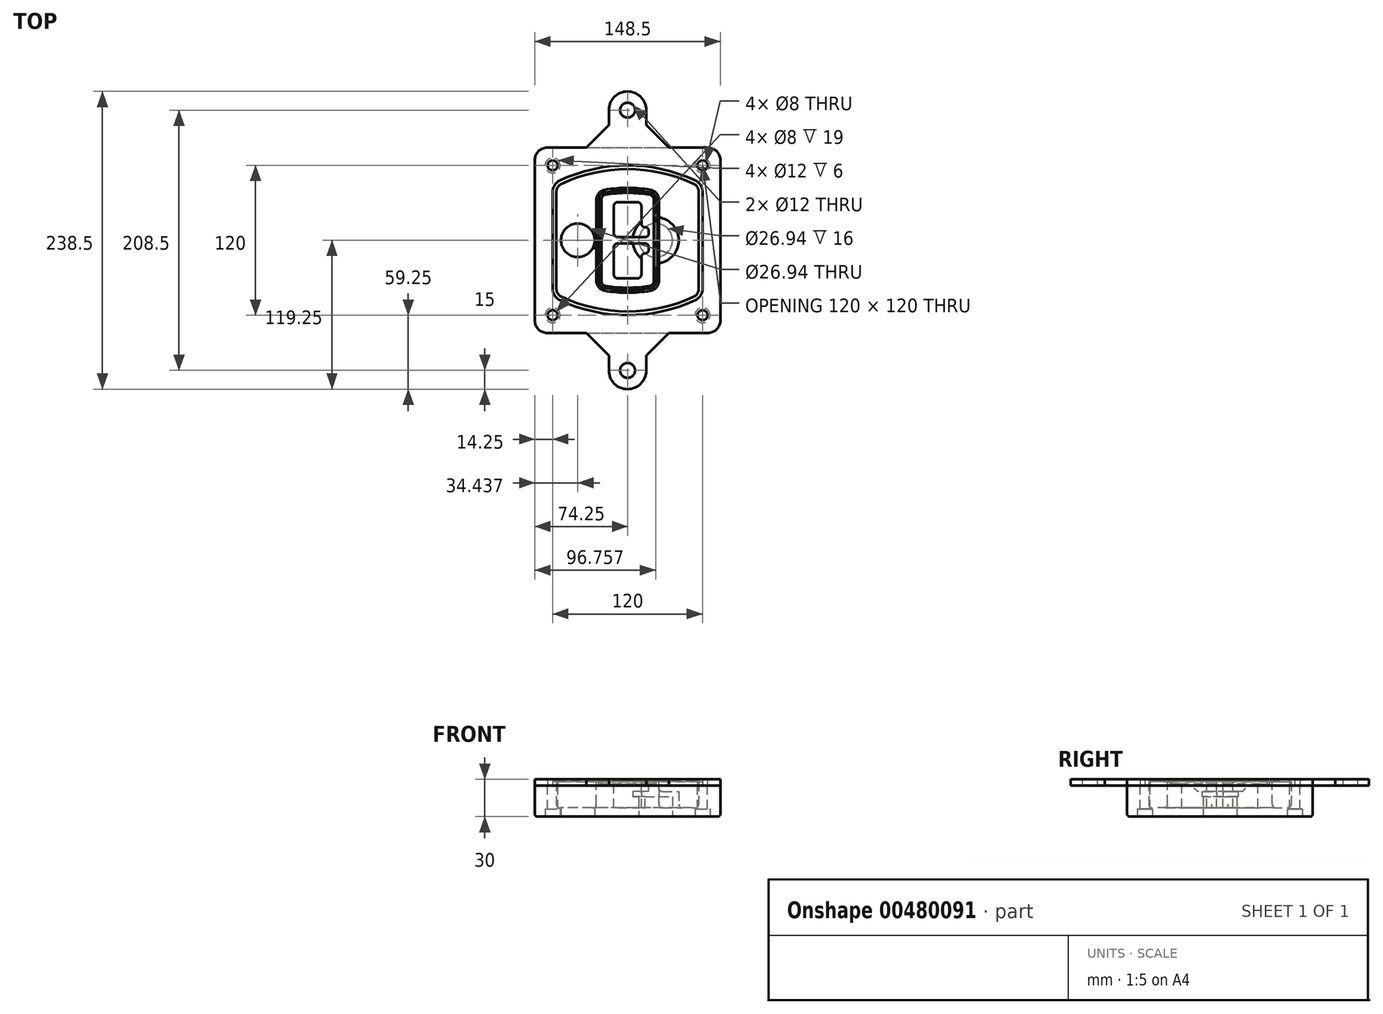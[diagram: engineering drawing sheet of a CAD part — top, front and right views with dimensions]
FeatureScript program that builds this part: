
annotation { "Feature Type Name" : "Feature", "Feature Type Description" : "" }
export const myFeature = defineFeature(function(context is Context, id is Id, definition is map)
    precondition{}
    {
        {
            var Q0;
            Q0=qCreatedBy(makeId("Top.planeOp"),FACE);
            var sketch = newSketch(context, id + "F0", { "sketchPlane" : qUnion([Q0])});
            skPoint(sketch, "E0.rect.middle", {"position": v(0, 0) * mm});
            skLineSegment(sketch, "E1.bottom", {"start": v(-64.25, -74.25) * mm, "end": v(64.25, -74.25) * mm});
            skLineSegment(sketch, "E1.top", {"start": v(-64.25, 74.25) * mm, "end": v(64.25, 74.25) * mm});
            skLineSegment(sketch, "E1.left", {"start": v(-74.25, -64.25) * mm, "end": v(-74.25, 64.25) * mm});
            skLineSegment(sketch, "E1.right", {"start": v(74.25, -64.25) * mm, "end": v(74.25, 64.25) * mm});
            skLineSegment(sketch, "E2", {"start": v(-74.25, 74.25) * mm, "end": v(74.25, -74.25) * mm, "construction": true});
            skLineSegment(sketch, "E3", {"start": v(74.25, 74.25) * mm, "end": v(-74.25, -74.25) * mm, "construction": true});
            skCircle(sketch, "E4", {"center": v(-60, 60) * mm, "radius": 4 * mm});
            skCircle(sketch, "E5", {"center": v(60, 60) * mm, "radius": 4 * mm});
            skCircle(sketch, "E6", {"center": v(60, -60) * mm, "radius": 4 * mm});
            skCircle(sketch, "E7", {"center": v(-60, -60) * mm, "radius": 4 * mm});
            skLineSegment(sketch, "E8", {"start": v(-60, 60) * mm, "end": v(60, 60) * mm, "construction": true});
            skLineSegment(sketch, "E9", {"start": v(60, 60) * mm, "end": v(60, -60) * mm, "construction": true});
            skLineSegment(sketch, "E10", {"start": v(60, -60) * mm, "end": v(-60, -60) * mm, "construction": true});
            skLineSegment(sketch, "E11", {"start": v(-60, -60) * mm, "end": v(-60, 60) * mm, "construction": true});
            skLineSegment(sketch, "E12", {"start": v(-60, 38.83) * mm, "end": v(-60, -38.83) * mm});
            skLineSegment(sketch, "E13", {"start": v(60, 38.83) * mm, "end": v(60, -38.83) * mm});
            skArc(sketch, "E14", {"start": v(54.26, 47.88) * mm, "mid": v(0, 60) * mm, "end": v(-54.26, 47.88) * mm});
            skArc(sketch, "E15", {"start": v(-54.26, -47.88) * mm, "mid": v(0, -60) * mm, "end": v(54.26, -47.88) * mm});
            skLineSegment(sketch, "E16", {"start": v(-60, 0) * mm, "end": v(60, 0) * mm, "construction": true});
            skPoint(sketch, "E17.visualSharp", {"position": v(-60, -45) * mm});
            skArc(sketch, "E17.filletArc", {"start": v(-60, -38.83) * mm, "mid": v(-58.44, -44.2) * mm, "end": v(-54.26, -47.88) * mm});
            skPoint(sketch, "E18.visualSharp", {"position": v(-60, 45) * mm});
            skArc(sketch, "E18.filletArc", {"start": v(-54.26, 47.88) * mm, "mid": v(-58.44, 44.2) * mm, "end": v(-60, 38.83) * mm});
            skPoint(sketch, "E19.visualSharp", {"position": v(60, 45) * mm});
            skArc(sketch, "E19.filletArc", {"start": v(60, 38.83) * mm, "mid": v(58.44, 44.2) * mm, "end": v(54.26, 47.88) * mm});
            skPoint(sketch, "E20.visualSharp", {"position": v(60, -45) * mm});
            skArc(sketch, "E20.filletArc", {"start": v(54.26, -47.88) * mm, "mid": v(58.44, -44.2) * mm, "end": v(60, -38.83) * mm});
            skPoint(sketch, "E21.visualSharp", {"position": v(-74.25, 74.25) * mm});
            skArc(sketch, "E21.filletArc", {"start": v(-64.25, 74.25) * mm, "mid": v(-71.32, 71.32) * mm, "end": v(-74.25, 64.25) * mm});
            skPoint(sketch, "E22.visualSharp", {"position": v(74.25, 74.25) * mm});
            skArc(sketch, "E22.filletArc", {"start": v(74.25, 64.25) * mm, "mid": v(71.32, 71.32) * mm, "end": v(64.25, 74.25) * mm});
            skPoint(sketch, "E23.visualSharp", {"position": v(74.25, -74.25) * mm});
            skArc(sketch, "E23.filletArc", {"start": v(64.25, -74.25) * mm, "mid": v(71.32, -71.32) * mm, "end": v(74.25, -64.25) * mm});
            skPoint(sketch, "E24.visualSharp", {"position": v(-74.25, -74.25) * mm});
            skArc(sketch, "E24.filletArc", {"start": v(-74.25, -64.25) * mm, "mid": v(-71.32, -71.32) * mm, "end": v(-64.25, -74.25) * mm});
            skArc(sketch, "E25.0", {"start": v(57, 38.83) * mm, "mid": v(55.9, 42.58) * mm, "end": v(52.98, 45.17) * mm});
            skLineSegment(sketch, "E25.1", {"start": v(57, 38.83) * mm, "end": v(57, -38.83) * mm});
            skArc(sketch, "E25.2", {"start": v(52.98, -45.17) * mm, "mid": v(55.9, -42.58) * mm, "end": v(57, -38.83) * mm});
            skArc(sketch, "E25.3", {"start": v(-52.98, -45.17) * mm, "mid": v(0, -57) * mm, "end": v(52.98, -45.17) * mm});
            skArc(sketch, "E25.4", {"start": v(-57, -38.83) * mm, "mid": v(-55.9, -42.58) * mm, "end": v(-52.98, -45.17) * mm});
            skArc(sketch, "E25.5", {"start": v(52.98, 45.17) * mm, "mid": v(0, 57) * mm, "end": v(-52.98, 45.17) * mm});
            skLineSegment(sketch, "E25.6", {"start": v(-57, 38.83) * mm, "end": v(-57, -38.83) * mm});
            skArc(sketch, "E25.7", {"start": v(-52.98, 45.17) * mm, "mid": v(-55.9, 42.58) * mm, "end": v(-57, 38.83) * mm});
            skArc(sketch, "E26.0", {"start": v(-55.96, 51.5) * mm, "mid": v(-61.82, 46.33) * mm, "end": v(-64, 38.83) * mm});
            skArc(sketch, "E26.1", {"start": v(55.96, 51.5) * mm, "mid": v(0, 64) * mm, "end": v(-55.96, 51.5) * mm});
            skArc(sketch, "E26.2", {"start": v(64, 38.83) * mm, "mid": v(61.82, 46.33) * mm, "end": v(55.96, 51.5) * mm});
            skLineSegment(sketch, "E26.3", {"start": v(64, 38.83) * mm, "end": v(64, -38.83) * mm});
            skArc(sketch, "E26.4", {"start": v(55.96, -51.5) * mm, "mid": v(61.82, -46.33) * mm, "end": v(64, -38.83) * mm});
            skLineSegment(sketch, "E26.5", {"start": v(-64, 38.83) * mm, "end": v(-64, -38.83) * mm});
            skArc(sketch, "E26.6", {"start": v(-55.96, -51.5) * mm, "mid": v(0, -64) * mm, "end": v(55.96, -51.5) * mm});
            skArc(sketch, "E26.7", {"start": v(-64, -38.83) * mm, "mid": v(-61.82, -46.33) * mm, "end": v(-55.96, -51.5) * mm});
            skSolve(sketch);
        }
        {
            var Q0;
            Q0=makeQuery(id+"F0.imprint","IMPRINT",FACE,{"disambiguationData":[TD([[makeQuery(id+"F0.imprint","IMPRINT",EDGE,{"derivedFrom":sQuery(id+"F0.wireOp",EDGE,"E1.bottom")}),1.0]])]});
            var Q1;
            Q1=makeQuery(id+"F0.imprint","IMPRINT",FACE,{"disambiguationData":[TD([[makeQuery(id+"F0.imprint","IMPRINT",EDGE,{"derivedFrom":sQuery(id+"F0.wireOp",EDGE,"E12")}),1.0]])]});
            var Q2;
            Q2=makeQuery(id+"F0.imprint","IMPRINT",FACE,{"disambiguationData":[TD([[makeQuery(id+"F0.imprint","IMPRINT",EDGE,{"derivedFrom":sQuery(id+"F0.wireOp",EDGE,"E25.0")}),1.0]])]});
            var Q3;
            Q3=makeQuery(id+"F0.imprint","IMPRINT",FACE,{"disambiguationData":[TD([[makeQuery(id+"F0.imprint","IMPRINT",EDGE,{"derivedFrom":sQuery(id+"F0.wireOp",EDGE,"E12")}),-1.0]])]});
            extrude(context, id + "F1", {"entities" : qUnion([Q0, Q1, Q2, Q3]), "oppositeDirection" : true, "depth" : 25 * mm});
        }
        {
            var Q0;
            Q0=makeQuery(id+"F0.imprint","IMPRINT",FACE,{"disambiguationData":[TD([[makeQuery(id+"F0.imprint","IMPRINT",EDGE,{"derivedFrom":sQuery(id+"F0.wireOp",EDGE,"E12")}),1.0]])]});
            extrude(context, id + "F2", {"entities" : qUnion([Q0]), "operationType" : NewBodyOperationType.ADD, "depth" : 3 * mm});
        }
        {
            var Q0;
            Q0=makeQuery(id+"F0.imprint","IMPRINT",FACE,{"disambiguationData":[TD([[makeQuery(id+"F0.imprint","IMPRINT",EDGE,{"derivedFrom":sQuery(id+"F0.wireOp",EDGE,"E25.0")}),1.0]])]});
            extrude(context, id + "F3", {"entities" : qUnion([Q0]), "operationType" : NewBodyOperationType.REMOVE, "oppositeDirection" : true, "depth" : 18 * mm});
        }
        {
            var Q0;
            Q0=makeQuery(id+"F2.opExtrude","CAP_FACE",FACE,{"disambiguationData":[OSD([sQuery(id+"F0.wireOp",EDGE,"E12"),sQuery(id+"F0.wireOp",EDGE,"E13"),sQuery(id+"F0.wireOp",EDGE,"E14"),sQuery(id+"F0.wireOp",EDGE,"E15"),sQuery(id+"F0.wireOp",EDGE,"E17.filletArc"),sQuery(id+"F0.wireOp",EDGE,"E18.filletArc"),sQuery(id+"F0.wireOp",EDGE,"E19.filletArc"),sQuery(id+"F0.wireOp",EDGE,"E20.filletArc"),sQuery(id+"F0.wireOp",EDGE,"E25.0"),sQuery(id+"F0.wireOp",EDGE,"E25.1"),sQuery(id+"F0.wireOp",EDGE,"E25.2"),sQuery(id+"F0.wireOp",EDGE,"E25.3"),sQuery(id+"F0.wireOp",EDGE,"E25.4"),sQuery(id+"F0.wireOp",EDGE,"E25.5"),sQuery(id+"F0.wireOp",EDGE,"E25.6"),sQuery(id+"F0.wireOp",EDGE,"E25.7")])],"isStart":false});
            var sketch = newSketch(context, id + "F4", { "sketchPlane" : qUnion([Q0])});
            skArc(sketch, "E27.0", {"start": v(-18.34, -40.45) * mm, "mid": v(0, -42) * mm, "end": v(18.34, -40.45) * mm});
            skArc(sketch, "E28.0", {"start": v(18.34, 40.45) * mm, "mid": v(0, 42) * mm, "end": v(-18.34, 40.45) * mm});
            skLineSegment(sketch, "E29", {"start": v(-25, 32.57) * mm, "end": v(-25, -32.57) * mm});
            skLineSegment(sketch, "E30", {"start": v(25, 32.57) * mm, "end": v(25, -32.57) * mm});
            skLineSegment(sketch, "E31", {"start": v(-25, 39.1) * mm, "end": v(25, 39.1) * mm, "construction": true});
            skLineSegment(sketch, "E32", {"start": v(-25, -39.1) * mm, "end": v(25, -39.1) * mm, "construction": true});
            skPoint(sketch, "E33.visualSharp", {"position": v(-25, 39.1) * mm});
            skArc(sketch, "E33.filletArc", {"start": v(-18.34, 40.45) * mm, "mid": v(-23.11, 37.73) * mm, "end": v(-25, 32.57) * mm});
            skPoint(sketch, "E34.visualSharp", {"position": v(25, 39.1) * mm});
            skArc(sketch, "E34.filletArc", {"start": v(25, 32.57) * mm, "mid": v(23.11, 37.73) * mm, "end": v(18.34, 40.45) * mm});
            skPoint(sketch, "E35.visualSharp", {"position": v(25, -39.1) * mm});
            skArc(sketch, "E35.filletArc", {"start": v(18.34, -40.45) * mm, "mid": v(23.11, -37.73) * mm, "end": v(25, -32.57) * mm});
            skPoint(sketch, "E36.visualSharp", {"position": v(-25, -39.1) * mm});
            skArc(sketch, "E36.filletArc", {"start": v(-25, -32.57) * mm, "mid": v(-23.11, -37.73) * mm, "end": v(-18.34, -40.45) * mm});
            skArc(sketch, "E37.0", {"start": v(52.98, 45.17) * mm, "mid": v(0, 57) * mm, "end": v(-52.98, 45.17) * mm});
            skArc(sketch, "E37.1", {"start": v(-52.98, 45.17) * mm, "mid": v(-55.9, 42.58) * mm, "end": v(-57, 38.83) * mm});
            skLineSegment(sketch, "E37.2", {"start": v(-57, 38.83) * mm, "end": v(-57, -38.83) * mm});
            skArc(sketch, "E37.3", {"start": v(-57, -38.83) * mm, "mid": v(-55.9, -42.58) * mm, "end": v(-52.98, -45.17) * mm});
            skArc(sketch, "E37.4", {"start": v(-52.98, -45.17) * mm, "mid": v(0, -57) * mm, "end": v(52.98, -45.17) * mm});
            skArc(sketch, "E37.5", {"start": v(52.98, -45.17) * mm, "mid": v(55.9, -42.58) * mm, "end": v(57, -38.83) * mm});
            skLineSegment(sketch, "E37.6", {"start": v(57, 38.83) * mm, "end": v(57, -38.83) * mm});
            skArc(sketch, "E37.7", {"start": v(57, 38.83) * mm, "mid": v(55.9, 42.58) * mm, "end": v(52.98, 45.17) * mm});
            skLineSegment(sketch, "E38.0", {"start": v(23, 32.57) * mm, "end": v(23, -32.57) * mm});
            skArc(sketch, "E38.1", {"start": v(18, -38.48) * mm, "mid": v(21.58, -36.44) * mm, "end": v(23, -32.57) * mm});
            skArc(sketch, "E38.2", {"start": v(-18, -38.48) * mm, "mid": v(0, -40) * mm, "end": v(18, -38.48) * mm});
            skArc(sketch, "E38.3", {"start": v(-23, -32.57) * mm, "mid": v(-21.58, -36.44) * mm, "end": v(-18, -38.48) * mm});
            skLineSegment(sketch, "E38.4", {"start": v(-23, 32.57) * mm, "end": v(-23, -32.57) * mm});
            skArc(sketch, "E38.5", {"start": v(23, 32.57) * mm, "mid": v(21.58, 36.44) * mm, "end": v(18, 38.48) * mm});
            skArc(sketch, "E38.6", {"start": v(-18, 38.48) * mm, "mid": v(-21.58, 36.44) * mm, "end": v(-23, 32.57) * mm});
            skArc(sketch, "E38.7", {"start": v(18, 38.48) * mm, "mid": v(0, 40) * mm, "end": v(-18, 38.48) * mm});
            skArc(sketch, "E39.0", {"start": v(21, 32.57) * mm, "mid": v(20.06, 35.15) * mm, "end": v(17.67, 36.5) * mm});
            skLineSegment(sketch, "E39.1", {"start": v(21, 32.57) * mm, "end": v(21, -32.57) * mm});
            skArc(sketch, "E39.2", {"start": v(17.67, -36.5) * mm, "mid": v(20.06, -35.15) * mm, "end": v(21, -32.57) * mm});
            skArc(sketch, "E39.3", {"start": v(-17.67, -36.5) * mm, "mid": v(0, -38) * mm, "end": v(17.67, -36.5) * mm});
            skArc(sketch, "E39.4", {"start": v(-21, -32.57) * mm, "mid": v(-20.06, -35.15) * mm, "end": v(-17.67, -36.5) * mm});
            skArc(sketch, "E39.5", {"start": v(17.67, 36.5) * mm, "mid": v(0, 38) * mm, "end": v(-17.67, 36.5) * mm});
            skLineSegment(sketch, "E39.6", {"start": v(-21, 32.57) * mm, "end": v(-21, -32.57) * mm});
            skArc(sketch, "E39.7", {"start": v(-17.67, 36.5) * mm, "mid": v(-20.06, 35.15) * mm, "end": v(-21, 32.57) * mm});
            skLineSegment(sketch, "E40", {"start": v(-25, 0) * mm, "end": v(25, 0) * mm, "construction": true});
            skLineSegment(sketch, "E41", {"start": v(-11, 5.5) * mm, "end": v(-11, 27.5) * mm});
            skLineSegment(sketch, "E42", {"start": v(-8, 30.5) * mm, "end": v(8, 30.5) * mm});
            skLineSegment(sketch, "E43", {"start": v(11, 27.5) * mm, "end": v(11, 13.5) * mm});
            skLineSegment(sketch, "E44", {"start": v(14, 10.5) * mm, "end": v(14, 10.5) * mm});
            skLineSegment(sketch, "E45", {"start": v(17, 7.5) * mm, "end": v(17, 5.5) * mm});
            skLineSegment(sketch, "E46", {"start": v(14, 2.5) * mm, "end": v(-8, 2.5) * mm});
            skPoint(sketch, "E47.visualSharp", {"position": v(-11, 30.5) * mm});
            skArc(sketch, "E47.filletArc", {"start": v(-8, 30.5) * mm, "mid": v(-10.12, 29.62) * mm, "end": v(-11, 27.5) * mm});
            skPoint(sketch, "E48.visualSharp", {"position": v(11, 30.5) * mm});
            skArc(sketch, "E48.filletArc", {"start": v(11, 27.5) * mm, "mid": v(10.12, 29.62) * mm, "end": v(8, 30.5) * mm});
            skPoint(sketch, "E49.visualSharp", {"position": v(11, 10.5) * mm});
            skArc(sketch, "E49.filletArc", {"start": v(11, 13.5) * mm, "mid": v(11.88, 11.38) * mm, "end": v(14, 10.5) * mm});
            skPoint(sketch, "E50.visualSharp", {"position": v(17, 10.5) * mm});
            skArc(sketch, "E50.filletArc", {"start": v(17, 7.5) * mm, "mid": v(16.12, 9.62) * mm, "end": v(14, 10.5) * mm});
            skPoint(sketch, "E51.visualSharp", {"position": v(17, 2.5) * mm});
            skArc(sketch, "E51.filletArc", {"start": v(14, 2.5) * mm, "mid": v(16.12, 3.38) * mm, "end": v(17, 5.5) * mm});
            skPoint(sketch, "E52.visualSharp", {"position": v(-11, 2.5) * mm});
            skArc(sketch, "E52.filletArc", {"start": v(-11, 5.5) * mm, "mid": v(-10.12, 3.38) * mm, "end": v(-8, 2.5) * mm});
            skLineSegment(sketch, "E53.0.MirrorCS", {"start": v(14, -2.5) * mm, "end": v(-8, -2.5) * mm});
            skArc(sketch, "E54.0.MirrorCS", {"start": v(-11, -5.5) * mm, "mid": v(-10.12, -3.38) * mm, "end": v(-8, -2.5) * mm});
            skLineSegment(sketch, "E55.0.MirrorCS", {"start": v(-11, -5.5) * mm, "end": v(-11, -27.5) * mm});
            skArc(sketch, "E56.0.MirrorCS", {"start": v(-8, -30.5) * mm, "mid": v(-10.12, -29.62) * mm, "end": v(-11, -27.5) * mm});
            skLineSegment(sketch, "E57.0.MirrorCS", {"start": v(-8, -30.5) * mm, "end": v(8, -30.5) * mm});
            skArc(sketch, "E58.0.MirrorCS", {"start": v(11, -27.5) * mm, "mid": v(10.12, -29.62) * mm, "end": v(8, -30.5) * mm});
            skLineSegment(sketch, "E59.0.MirrorCS", {"start": v(11, -27.5) * mm, "end": v(11, -13.5) * mm});
            skArc(sketch, "E60.0.MirrorCS", {"start": v(11, -13.5) * mm, "mid": v(11.88, -11.38) * mm, "end": v(14, -10.5) * mm});
            skArc(sketch, "E61.0.MirrorCS", {"start": v(17, -7.5) * mm, "mid": v(16.12, -9.62) * mm, "end": v(14, -10.5) * mm});
            skLineSegment(sketch, "E62.0.MirrorCS", {"start": v(17, -7.5) * mm, "end": v(17, -5.5) * mm});
            skArc(sketch, "E63.0.MirrorCS", {"start": v(14, -2.5) * mm, "mid": v(16.12, -3.38) * mm, "end": v(17, -5.5) * mm});
            skSolve(sketch);
        }
        {
            var Q0;
            Q0=makeQuery(id+"F4.imprint","IMPRINT",FACE,{"disambiguationData":[TD([[makeQuery(id+"F4.imprint","IMPRINT",EDGE,{"derivedFrom":sQuery(id+"F4.wireOp",EDGE,"E27.0")}),1.0]])]});
            var Q1;
            Q1=makeQuery(id+"F4.imprint","IMPRINT",FACE,{"disambiguationData":[TD([[makeQuery(id+"F4.imprint","IMPRINT",EDGE,{"derivedFrom":sQuery(id+"F4.wireOp",EDGE,"E38.0")}),-1.0]])]});
            var Q2;
            Q2=makeQuery(id+"F4.imprint","IMPRINT",FACE,{"disambiguationData":[TD([[makeQuery(id+"F4.imprint","IMPRINT",EDGE,{"derivedFrom":sQuery(id+"F4.wireOp",EDGE,"E39.0")}),1.0]])]});
            extrude(context, id + "F5", {"entities" : qUnion([Q0, Q1, Q2]), "operationType" : NewBodyOperationType.ADD, "endBound" : BoundingType.UP_TO_NEXT, "oppositeDirection" : true, "depth" : 25 * mm});
        }
        {
            var Q0;
            Q0=makeQuery(id+"F4.imprint","IMPRINT",FACE,{"disambiguationData":[TD([[makeQuery(id+"F4.imprint","IMPRINT",EDGE,{"derivedFrom":sQuery(id+"F4.wireOp",EDGE,"E38.0")}),-1.0]])]});
            extrude(context, id + "F6", {"entities" : qUnion([Q0]), "operationType" : NewBodyOperationType.REMOVE, "oppositeDirection" : true, "depth" : 2 * mm});
        }
        {
            var Q0;
            Q0=makeQuery(id+"F1.opExtrude","CAP_FACE",FACE,{"disambiguationData":[OSD([sQuery(id+"F0.wireOp",EDGE,"E1.bottom"),sQuery(id+"F0.wireOp",EDGE,"E1.top"),sQuery(id+"F0.wireOp",EDGE,"E1.left"),sQuery(id+"F0.wireOp",EDGE,"E1.right"),sQuery(id+"F0.wireOp",EDGE,"E4"),sQuery(id+"F0.wireOp",EDGE,"E5"),sQuery(id+"F0.wireOp",EDGE,"E6"),sQuery(id+"F0.wireOp",EDGE,"E7"),sQuery(id+"F0.wireOp",EDGE,"E21.filletArc"),sQuery(id+"F0.wireOp",EDGE,"E22.filletArc"),sQuery(id+"F0.wireOp",EDGE,"E23.filletArc"),sQuery(id+"F0.wireOp",EDGE,"E24.filletArc")])],"isStart":false});
            var sketch = newSketch(context, id + "F7", { "sketchPlane" : qUnion([Q0])});
            skCircle(sketch, "E64", {"center": v(22.5, 0) * mm, "radius": 13.47 * mm});
            skCircle(sketch, "E65", {"center": v(-39.81, 0) * mm, "radius": 13.47 * mm});
            skLineSegment(sketch, "E66", {"start": v(74.25, 0) * mm, "end": v(-74.25, 0) * mm});
            skCircle(sketch, "E67", {"center": v(22.5, 0) * mm, "radius": 18.47 * mm});
            skCircle(sketch, "E68", {"center": v(60, -60) * mm, "radius": 6 * mm});
            skCircle(sketch, "E69", {"center": v(-60, -60) * mm, "radius": 6 * mm});
            skCircle(sketch, "E70", {"center": v(-60, 60) * mm, "radius": 6 * mm});
            skCircle(sketch, "E71", {"center": v(60, 60) * mm, "radius": 6 * mm});
            skSolve(sketch);
        }
        {
            var Q0;
            {var subQ1=sQuery(id+"F7.wireOp",EDGE,"E66");var subQ4=sQuery(id+"F7.wireOp",EDGE,"E64");var subQ6=makeQuery(id+"F7.imprint","INTERSECT",VERTEX,{"disambiguationData":[OD(0.0)],"derivedFrom":[subQ4,subQ1]});Q0=makeQuery(id+"F7.imprint","IMPRINT",FACE,{"disambiguationData":[TD([[makeQuery(id+"F7.imprint","IMPRINT",EDGE,{"disambiguationData":[TD([[subQ6,-1.0]])],"derivedFrom":subQ4}),-1.0]])]});}
            var Q1;
            {var subQ0=sQuery(id+"F7.wireOp",EDGE,"E66");var subQ1=sQuery(id+"F7.wireOp",EDGE,"E64");var subQ3=makeQuery(id+"F7.imprint","INTERSECT",VERTEX,{"disambiguationData":[OD(0.0)],"derivedFrom":[subQ1,subQ0]});Q1=makeQuery(id+"F7.imprint","IMPRINT",FACE,{"disambiguationData":[TD([[makeQuery(id+"F7.imprint","IMPRINT",EDGE,{"disambiguationData":[TD([[subQ3,-1.0]])],"derivedFrom":subQ1}),1.0]])]});}
            var Q2;
            {var subQ0=sQuery(id+"F7.wireOp",EDGE,"E66");var subQ1=sQuery(id+"F7.wireOp",EDGE,"E64");var subQ3=makeQuery(id+"F7.imprint","INTERSECT",VERTEX,{"disambiguationData":[OD(0.0)],"derivedFrom":[subQ1,subQ0]});Q2=makeQuery(id+"F7.imprint","IMPRINT",FACE,{"disambiguationData":[TD([[makeQuery(id+"F7.imprint","IMPRINT",EDGE,{"disambiguationData":[TD([[subQ3,1.0]])],"derivedFrom":subQ1}),1.0]])]});}
            var Q3;
            {var subQ1=sQuery(id+"F7.wireOp",EDGE,"E66");var subQ4=sQuery(id+"F7.wireOp",EDGE,"E64");var subQ6=makeQuery(id+"F7.imprint","INTERSECT",VERTEX,{"disambiguationData":[OD(0.0)],"derivedFrom":[subQ4,subQ1]});Q3=makeQuery(id+"F7.imprint","IMPRINT",FACE,{"disambiguationData":[TD([[makeQuery(id+"F7.imprint","IMPRINT",EDGE,{"disambiguationData":[TD([[subQ6,1.0]])],"derivedFrom":subQ4}),-1.0]])]});}
            extrude(context, id + "F8", {"entities" : qUnion([Q0, Q1, Q2, Q3]), "operationType" : NewBodyOperationType.ADD, "oppositeDirection" : true, "depth" : 20 * mm});
        }
        {
            var Q0;
            {var subQ0=sQuery(id+"F7.wireOp",EDGE,"E66");var subQ1=sQuery(id+"F7.wireOp",EDGE,"E64");var subQ3=makeQuery(id+"F7.imprint","INTERSECT",VERTEX,{"disambiguationData":[OD(0.0)],"derivedFrom":[subQ1,subQ0]});Q0=makeQuery(id+"F7.imprint","IMPRINT",FACE,{"disambiguationData":[TD([[makeQuery(id+"F7.imprint","IMPRINT",EDGE,{"disambiguationData":[TD([[subQ3,-1.0]])],"derivedFrom":subQ1}),1.0]])]});}
            var Q1;
            {var subQ0=sQuery(id+"F7.wireOp",EDGE,"E66");var subQ1=sQuery(id+"F7.wireOp",EDGE,"E64");var subQ3=makeQuery(id+"F7.imprint","INTERSECT",VERTEX,{"disambiguationData":[OD(0.0)],"derivedFrom":[subQ1,subQ0]});Q1=makeQuery(id+"F7.imprint","IMPRINT",FACE,{"disambiguationData":[TD([[makeQuery(id+"F7.imprint","IMPRINT",EDGE,{"disambiguationData":[TD([[subQ3,1.0]])],"derivedFrom":subQ1}),1.0]])]});}
            extrude(context, id + "F9", {"entities" : qUnion([Q0, Q1]), "operationType" : NewBodyOperationType.REMOVE, "oppositeDirection" : true, "depth" : 16 * mm});
        }
        {
            var Q0;
            {var subQ0=sQuery(id+"F7.wireOp",EDGE,"E66");var subQ1=sQuery(id+"F7.wireOp",EDGE,"E65");var subQ3=makeQuery(id+"F7.imprint","INTERSECT",VERTEX,{"disambiguationData":[OD(0.0)],"derivedFrom":[subQ1,subQ0]});Q0=makeQuery(id+"F7.imprint","IMPRINT",FACE,{"disambiguationData":[TD([[makeQuery(id+"F7.imprint","IMPRINT",EDGE,{"disambiguationData":[TD([[subQ3,-1.0]])],"derivedFrom":subQ1}),1.0]])]});}
            var Q1;
            {var subQ0=sQuery(id+"F7.wireOp",EDGE,"E66");var subQ1=sQuery(id+"F7.wireOp",EDGE,"E65");var subQ3=makeQuery(id+"F7.imprint","INTERSECT",VERTEX,{"disambiguationData":[OD(0.0)],"derivedFrom":[subQ1,subQ0]});Q1=makeQuery(id+"F7.imprint","IMPRINT",FACE,{"disambiguationData":[TD([[makeQuery(id+"F7.imprint","IMPRINT",EDGE,{"disambiguationData":[TD([[subQ3,1.0]])],"derivedFrom":subQ1}),1.0]])]});}
            extrude(context, id + "F10", {"entities" : qUnion([Q0, Q1]), "operationType" : NewBodyOperationType.REMOVE, "oppositeDirection" : true, "depth" : 25 * mm});
        }
        {
            var Q0;
            Q0=makeQuery(id+"F7.imprint","IMPRINT",FACE,{"disambiguationData":[TD([[makeQuery(id+"F7.imprint","IMPRINT",EDGE,{"derivedFrom":sQuery(id+"F7.wireOp",EDGE,"E68")}),1.0]])]});
            var Q1;
            Q1=makeQuery(id+"F7.imprint","IMPRINT",FACE,{"disambiguationData":[TD([[makeQuery(id+"F7.imprint","IMPRINT",EDGE,{"derivedFrom":makeQuery(id+"F1.opExtrude","CAP_EDGE",EDGE,{"disambiguationData":[OSD([sQuery(id+"F0.wireOp",EDGE,"E5")])],"isStart":false})}),-1.0]])]});
            var Q2;
            Q2=makeQuery(id+"F7.imprint","IMPRINT",FACE,{"disambiguationData":[TD([[makeQuery(id+"F7.imprint","IMPRINT",EDGE,{"derivedFrom":sQuery(id+"F7.wireOp",EDGE,"E69")}),1.0]])]});
            var Q3;
            Q3=makeQuery(id+"F7.imprint","IMPRINT",FACE,{"disambiguationData":[TD([[makeQuery(id+"F7.imprint","IMPRINT",EDGE,{"derivedFrom":makeQuery(id+"F1.opExtrude","CAP_EDGE",EDGE,{"disambiguationData":[OSD([sQuery(id+"F0.wireOp",EDGE,"E4")])],"isStart":false})}),-1.0]])]});
            var Q4;
            Q4=makeQuery(id+"F7.imprint","IMPRINT",FACE,{"disambiguationData":[TD([[makeQuery(id+"F7.imprint","IMPRINT",EDGE,{"derivedFrom":sQuery(id+"F7.wireOp",EDGE,"E70")}),1.0]])]});
            var Q5;
            Q5=makeQuery(id+"F7.imprint","IMPRINT",FACE,{"disambiguationData":[TD([[makeQuery(id+"F7.imprint","IMPRINT",EDGE,{"derivedFrom":makeQuery(id+"F1.opExtrude","CAP_EDGE",EDGE,{"disambiguationData":[OSD([sQuery(id+"F0.wireOp",EDGE,"E7")])],"isStart":false})}),-1.0]])]});
            var Q6;
            Q6=makeQuery(id+"F7.imprint","IMPRINT",FACE,{"disambiguationData":[TD([[makeQuery(id+"F7.imprint","IMPRINT",EDGE,{"derivedFrom":sQuery(id+"F7.wireOp",EDGE,"E71")}),1.0]])]});
            var Q7;
            Q7=makeQuery(id+"F7.imprint","IMPRINT",FACE,{"disambiguationData":[TD([[makeQuery(id+"F7.imprint","IMPRINT",EDGE,{"derivedFrom":makeQuery(id+"F1.opExtrude","CAP_EDGE",EDGE,{"disambiguationData":[OSD([sQuery(id+"F0.wireOp",EDGE,"E6")])],"isStart":false})}),-1.0]])]});
            extrude(context, id + "F11", {"entities" : qUnion([Q0, Q1, Q2, Q3, Q4, Q5, Q6, Q7]), "operationType" : NewBodyOperationType.REMOVE, "oppositeDirection" : true, "depth" : 6 * mm});
        }
        {
            var Q0;
            Q0=makeQuery(id+"F9.boolean.opBoolean","COPY",FACE,{"derivedFrom":makeQuery(id+"F9.opExtrude","CAP_FACE",FACE,{"disambiguationData":[OSD([sQuery(id+"F7.wireOp",EDGE,"E64")])],"isStart":false})});
            var sketch = newSketch(context, id + "F12", { "sketchPlane" : qUnion([Q0])});
            skArc(sketch, "E72.0", {"start": v(11, 14.45) * mm, "mid": v(6.45, 9.13) * mm, "end": v(4.2, 2.5) * mm});
            skArc(sketch, "E72.1", {"start": v(4.2, -2.5) * mm, "mid": v(6.45, -9.13) * mm, "end": v(11, -14.45) * mm});
            skLineSegment(sketch, "E73", {"start": v(4.2, -2.5) * mm, "end": v(14, -2.5) * mm});
            skLineSegment(sketch, "E74.0", {"start": v(14, 2.5) * mm, "end": v(4.2, 2.5) * mm});
            skArc(sketch, "E74.1", {"start": v(14, 2.5) * mm, "mid": v(16.12, 3.38) * mm, "end": v(17, 5.5) * mm});
            skLineSegment(sketch, "E74.2", {"start": v(17, 7.5) * mm, "end": v(17, 5.5) * mm});
            skArc(sketch, "E74.3", {"start": v(17, 7.5) * mm, "mid": v(16.12, 9.62) * mm, "end": v(14, 10.5) * mm});
            skArc(sketch, "E74.4", {"start": v(11, 13.5) * mm, "mid": v(11.88, 11.38) * mm, "end": v(14, 10.5) * mm});
            skLineSegment(sketch, "E74.5", {"start": v(11, 14.45) * mm, "end": v(11, 13.5) * mm});
            skLineSegment(sketch, "E74.7", {"start": v(14, -2.5) * mm, "end": v(4.2, -2.5) * mm});
            skArc(sketch, "E74.8", {"start": v(14, -2.5) * mm, "mid": v(16.12, -3.38) * mm, "end": v(17, -5.5) * mm});
            skLineSegment(sketch, "E74.9", {"start": v(17, -7.5) * mm, "end": v(17, -5.5) * mm});
            skArc(sketch, "E74.10", {"start": v(17, -7.5) * mm, "mid": v(16.12, -9.62) * mm, "end": v(14, -10.5) * mm});
            skArc(sketch, "E74.11", {"start": v(11, -13.5) * mm, "mid": v(11.88, -11.38) * mm, "end": v(14, -10.5) * mm});
            skLineSegment(sketch, "E74.12", {"start": v(11, -14.45) * mm, "end": v(11, -13.5) * mm});
            skPoint(sketch, "E75.orphan", {"position": v(11, -27.5) * mm});
            skPoint(sketch, "E76.orphan", {"position": v(-8, -2.5) * mm});
            skPoint(sketch, "E77.orphan", {"position": v(-8, 2.5) * mm});
            skPoint(sketch, "E78.orphan", {"position": v(11, 27.5) * mm});
            skSolve(sketch);
        }
        {
            var Q0;
            {var subQ7=sQuery(id+"F12.wireOp",EDGE,"E72.0");var subQ14=sQuery(id+"F12.wireOp",EDGE,"E72.1");var subQ16=sQuery(id+"F12.wireOp",EDGE,"E74.1");var subQ18=sQuery(id+"F12.wireOp",EDGE,"E74.8");Q0=qUnion([makeQuery(id+"F12.imprint","IMPRINT",FACE,{"disambiguationData":[TD([[makeQuery(id+"F12.imprint","IMPRINT",EDGE,{"derivedFrom":subQ7}),1.0]])]}),makeQuery(id+"F12.imprint","IMPRINT",FACE,{"disambiguationData":[TD([[makeQuery(id+"F12.imprint","IMPRINT",EDGE,{"derivedFrom":subQ14}),1.0]])]}),makeQuery(id+"F12.imprint","IMPRINT",FACE,{"disambiguationData":[TD([[makeQuery(id+"F12.imprint","IMPRINT",EDGE,{"derivedFrom":subQ16}),1.0]])]}),makeQuery(id+"F12.imprint","IMPRINT",FACE,{"disambiguationData":[TD([[makeQuery(id+"F12.imprint","IMPRINT",EDGE,{"derivedFrom":subQ18}),-1.0]])]})]);}
            var Q1;
            Q1=makeQuery(id+"F5.boolean.opBoolean","SPLIT",FACE,{"disambiguationData":[TD([makeQuery(id+"F5.opExtrude","SWEPT_FACE",FACE,{"disambiguationData":[OSD([sQuery(id+"F4.wireOp",EDGE,"E41")])]})])],"derivedFrom":makeQuery(id+"F3.boolean.opBoolean","COPY",FACE,{"derivedFrom":makeQuery(id+"F3.opExtrude","CAP_FACE",FACE,{"disambiguationData":[OSD([sQuery(id+"F0.wireOp",EDGE,"E25.0"),sQuery(id+"F0.wireOp",EDGE,"E25.1"),sQuery(id+"F0.wireOp",EDGE,"E25.2"),sQuery(id+"F0.wireOp",EDGE,"E25.3"),sQuery(id+"F0.wireOp",EDGE,"E25.4"),sQuery(id+"F0.wireOp",EDGE,"E25.5"),sQuery(id+"F0.wireOp",EDGE,"E25.6"),sQuery(id+"F0.wireOp",EDGE,"E25.7")])],"isStart":false})})});
            extrude(context, id + "F13", {"entities" : qUnion([Q0]), "operationType" : NewBodyOperationType.REMOVE, "endBound" : BoundingType.UP_TO_SURFACE, "endBoundEntityFace" : qUnion([Q1]), "depth" : 25 * mm});
        }
        {
            var Q0;
            Q0=makeQuery(id+"F3.boolean.opBoolean","COPY",EDGE,{"derivedFrom":makeQuery(id+"F3.opExtrude","CAP_EDGE",EDGE,{"disambiguationData":[OSD([sQuery(id+"F0.wireOp",EDGE,"E25.6")])],"isStart":false})});
            var Q1;
            Q1=makeQuery(id+"F8.boolean.opBoolean","INTERSECT",EDGE,{"derivedFrom":[makeQuery(id+"F5.opExtrude","SWEPT_FACE",FACE,{"disambiguationData":[OSD([sQuery(id+"F4.wireOp",EDGE,"E30")])]}),makeQuery(id+"F8.opExtrude","CAP_FACE",FACE,{"disambiguationData":[OSD([sQuery(id+"F7.wireOp",EDGE,"E67")])],"isStart":false})]});
            var Q2;
            Q2=makeQuery(id+"F8.boolean.opBoolean","INTERSECT",EDGE,{"disambiguationData":[OD(1.0)],"derivedFrom":[makeQuery(id+"F5.opExtrude","SWEPT_FACE",FACE,{"disambiguationData":[OSD([sQuery(id+"F4.wireOp",EDGE,"E30")])]}),makeQuery(id+"F8.opExtrude","SWEPT_FACE",FACE,{"disambiguationData":[OSD([sQuery(id+"F7.wireOp",EDGE,"E67")])]})]});
            var Q3;
            {var subQ0=sQuery(id+"F4.wireOp",EDGE,"E30");Q3=makeQuery(id+"F8.boolean.opBoolean","SPLIT",EDGE,{"disambiguationData":[TD([makeQuery(id+"F5.opExtrude","SWEPT_FACE",FACE,{"disambiguationData":[OSD([sQuery(id+"F4.wireOp",EDGE,"E35.filletArc")])]})])],"derivedFrom":makeQuery(id+"F5.opExtrude","CAP_EDGE",EDGE,{"disambiguationData":[OSD([subQ0])],"isStart":false})});}
            var Q4;
            {var subQ0=sQuery(id+"F0.wireOp",EDGE,"E25.7");var subQ1=sQuery(id+"F0.wireOp",EDGE,"E25.1");var subQ2=sQuery(id+"F0.wireOp",EDGE,"E25.6");var subQ3=sQuery(id+"F0.wireOp",EDGE,"E25.5");var subQ4=sQuery(id+"F0.wireOp",EDGE,"E25.4");var subQ5=sQuery(id+"F0.wireOp",EDGE,"E25.0");var subQ6=sQuery(id+"F0.wireOp",EDGE,"E25.2");var subQ7=sQuery(id+"F0.wireOp",EDGE,"E25.3");Q4=makeQuery(id+"F8.boolean.opBoolean","INTERSECT",EDGE,{"derivedFrom":[makeQuery(id+"F5.boolean.opBoolean","SPLIT",FACE,{"disambiguationData":[TD([makeQuery(id+"F2.opExtrude","SWEPT_FACE",FACE,{"disambiguationData":[OSD([subQ5])]})])],"derivedFrom":makeQuery(id+"F3.boolean.opBoolean","COPY",FACE,{"derivedFrom":makeQuery(id+"F3.opExtrude","CAP_FACE",FACE,{"disambiguationData":[OSD([subQ5,subQ1,subQ6,subQ7,subQ4,subQ3,subQ2,subQ0])],"isStart":false})})}),makeQuery(id+"F8.opExtrude","SWEPT_FACE",FACE,{"disambiguationData":[OSD([sQuery(id+"F7.wireOp",EDGE,"E67")])]})]});}
            var Q5;
            Q5=makeQuery(id+"F8.boolean.opBoolean","INTERSECT",EDGE,{"disambiguationData":[OD(0.0)],"derivedFrom":[makeQuery(id+"F5.opExtrude","SWEPT_FACE",FACE,{"disambiguationData":[OSD([sQuery(id+"F4.wireOp",EDGE,"E30")])]}),makeQuery(id+"F8.opExtrude","SWEPT_FACE",FACE,{"disambiguationData":[OSD([sQuery(id+"F7.wireOp",EDGE,"E67")])]})]});
            fillet(context, id + "F14", {"entities" : qUnion([Q0, Q1, Q2, Q3, Q4, Q5]), "radius" : 3 * mm, "tangentPropagation" : true, "allowEdgeOverflow" : false});
        }
        {
            var Q0;
            Q0=makeQuery(id+"F1.opExtrude","CAP_EDGE",EDGE,{"disambiguationData":[OSD([sQuery(id+"F0.wireOp",EDGE,"E1.bottom")])],"isStart":false});
            fillet(context, id + "F15", {"entities" : qUnion([Q0]), "radius" : 2 * mm, "tangentPropagation" : true, "allowEdgeOverflow" : false});
        }
        {
            var Q0;
            {var subQ0=sQuery(id+"F0.wireOp",EDGE,"E21.filletArc");var subQ1=sQuery(id+"F0.wireOp",EDGE,"E7");var subQ2=sQuery(id+"F0.wireOp",EDGE,"E6");var subQ3=sQuery(id+"F0.wireOp",EDGE,"E5");var subQ4=sQuery(id+"F0.wireOp",EDGE,"E4");var subQ5=sQuery(id+"F0.wireOp",EDGE,"E22.filletArc");var subQ6=sQuery(id+"F0.wireOp",EDGE,"E1.bottom");var subQ7=sQuery(id+"F0.wireOp",EDGE,"E1.right");var subQ8=sQuery(id+"F0.wireOp",EDGE,"E1.top");var subQ9=sQuery(id+"F0.wireOp",EDGE,"E1.left");var subQ10=sQuery(id+"F0.wireOp",EDGE,"E23.filletArc");var subQ11=sQuery(id+"F0.wireOp",EDGE,"E24.filletArc");Q0=makeQuery(id+"F2.boolean.opBoolean","SPLIT",FACE,{"disambiguationData":[TD([makeQuery(id+"F1.opExtrude","SWEPT_FACE",FACE,{"disambiguationData":[OSD([subQ6])]})])],"derivedFrom":makeQuery(id+"F1.opExtrude","CAP_FACE",FACE,{"disambiguationData":[OSD([subQ6,subQ8,subQ9,subQ7,subQ4,subQ3,subQ2,subQ1,subQ0,subQ5,subQ10,subQ11])],"isStart":true})});}
            var sketch = newSketch(context, id + "F16", { "sketchPlane" : qUnion([Q0])});
            skLineSegment(sketch, "E79.0", {"start": v(-64.25, 74.25) * mm, "end": v(64.25, 74.25) * mm});
            skArc(sketch, "E79.1", {"start": v(-64.25, 74.25) * mm, "mid": v(-71.32, 71.32) * mm, "end": v(-74.25, 64.25) * mm});
            skLineSegment(sketch, "E79.2", {"start": v(-74.25, -64.25) * mm, "end": v(-74.25, 64.25) * mm});
            skArc(sketch, "E79.3", {"start": v(-74.25, -64.25) * mm, "mid": v(-71.32, -71.32) * mm, "end": v(-64.25, -74.25) * mm});
            skLineSegment(sketch, "E79.4", {"start": v(-64.25, -74.25) * mm, "end": v(64.25, -74.25) * mm});
            skArc(sketch, "E79.5", {"start": v(64.25, -74.25) * mm, "mid": v(71.32, -71.32) * mm, "end": v(74.25, -64.25) * mm});
            skLineSegment(sketch, "E79.6", {"start": v(74.25, -64.25) * mm, "end": v(74.25, 64.25) * mm});
            skArc(sketch, "E79.7", {"start": v(74.25, 64.25) * mm, "mid": v(71.32, 71.32) * mm, "end": v(64.25, 74.25) * mm});
            skArc(sketch, "E79.8", {"start": v(54.26, 47.88) * mm, "mid": v(0, 60) * mm, "end": v(-54.26, 47.88) * mm});
            skArc(sketch, "E79.9", {"start": v(60, 38.83) * mm, "mid": v(58.44, 44.2) * mm, "end": v(54.26, 47.88) * mm});
            skLineSegment(sketch, "E79.10", {"start": v(60, 38.83) * mm, "end": v(60, -38.83) * mm});
            skArc(sketch, "E79.11", {"start": v(-54.26, -47.88) * mm, "mid": v(0, -60) * mm, "end": v(54.26, -47.88) * mm});
            skArc(sketch, "E79.12", {"start": v(54.26, -47.88) * mm, "mid": v(58.44, -44.2) * mm, "end": v(60, -38.83) * mm});
            skLineSegment(sketch, "E79.13", {"start": v(-60, 38.83) * mm, "end": v(-60, -38.83) * mm});
            skArc(sketch, "E79.14", {"start": v(-60, -38.83) * mm, "mid": v(-58.44, -44.2) * mm, "end": v(-54.26, -47.88) * mm});
            skCircle(sketch, "E79.15", {"center": v(-60, 60) * mm, "radius": 4 * mm});
            skCircle(sketch, "E79.16", {"center": v(-60, -60) * mm, "radius": 4 * mm});
            skCircle(sketch, "E79.17", {"center": v(60, -60) * mm, "radius": 4 * mm});
            skCircle(sketch, "E79.18", {"center": v(60, 60) * mm, "radius": 4 * mm});
            skArc(sketch, "E79.19", {"start": v(-54.26, 47.88) * mm, "mid": v(-58.44, 44.2) * mm, "end": v(-60, 38.83) * mm});
            skLineSegment(sketch, "E80", {"start": v(0, 74.25) * mm, "end": v(0, 104.25) * mm, "construction": true});
            skCircle(sketch, "E81", {"center": v(0, 104.25) * mm, "radius": 6 * mm});
            skLineSegment(sketch, "E82", {"start": v(-15, 92.25) * mm, "end": v(-15, 104.25) * mm});
            skLineSegment(sketch, "E83", {"start": v(15, 92.25) * mm, "end": v(15, 104.25) * mm});
            skArc(sketch, "E84", {"start": v(15, 104.25) * mm, "mid": v(0, 119.25) * mm, "end": v(-15, 104.25) * mm});
            skLineSegment(sketch, "E85", {"start": v(-15, 92.25) * mm, "end": v(-33, 74.25) * mm});
            skLineSegment(sketch, "E86", {"start": v(15, 92.25) * mm, "end": v(33, 74.25) * mm});
            skLineSegment(sketch, "E87", {"start": v(-74.25, 0) * mm, "end": v(74.25, 0) * mm, "construction": true});
            skLineSegment(sketch, "E88.MirrorCS", {"start": v(-15, -92.25) * mm, "end": v(-33, -74.25) * mm});
            skLineSegment(sketch, "E89.MirrorCS", {"start": v(15, -92.25) * mm, "end": v(33, -74.25) * mm});
            skLineSegment(sketch, "E90.MirrorCS", {"start": v(15, -92.25) * mm, "end": v(15, -104.25) * mm});
            skLineSegment(sketch, "E91.MirrorCS", {"start": v(0, -74.25) * mm, "end": v(0, -104.25) * mm, "construction": true});
            skLineSegment(sketch, "E92.MirrorCS", {"start": v(-15, -92.25) * mm, "end": v(-15, -104.25) * mm});
            skCircle(sketch, "E93.MirrorC", {"center": v(0, -104.25) * mm, "radius": 6 * mm});
            skArc(sketch, "E94.MirrorCS", {"start": v(15, -104.25) * mm, "mid": v(0, -119.25) * mm, "end": v(-15, -104.25) * mm});
            skSolve(sketch);
        }
        {
            var Q0;
            Q0 = qSketchRegion(id + "F16", true);
            extrude(context, id + "F17", {"entities" : qUnion([Q0]), "depth" : 5 * mm});
        }
    });
